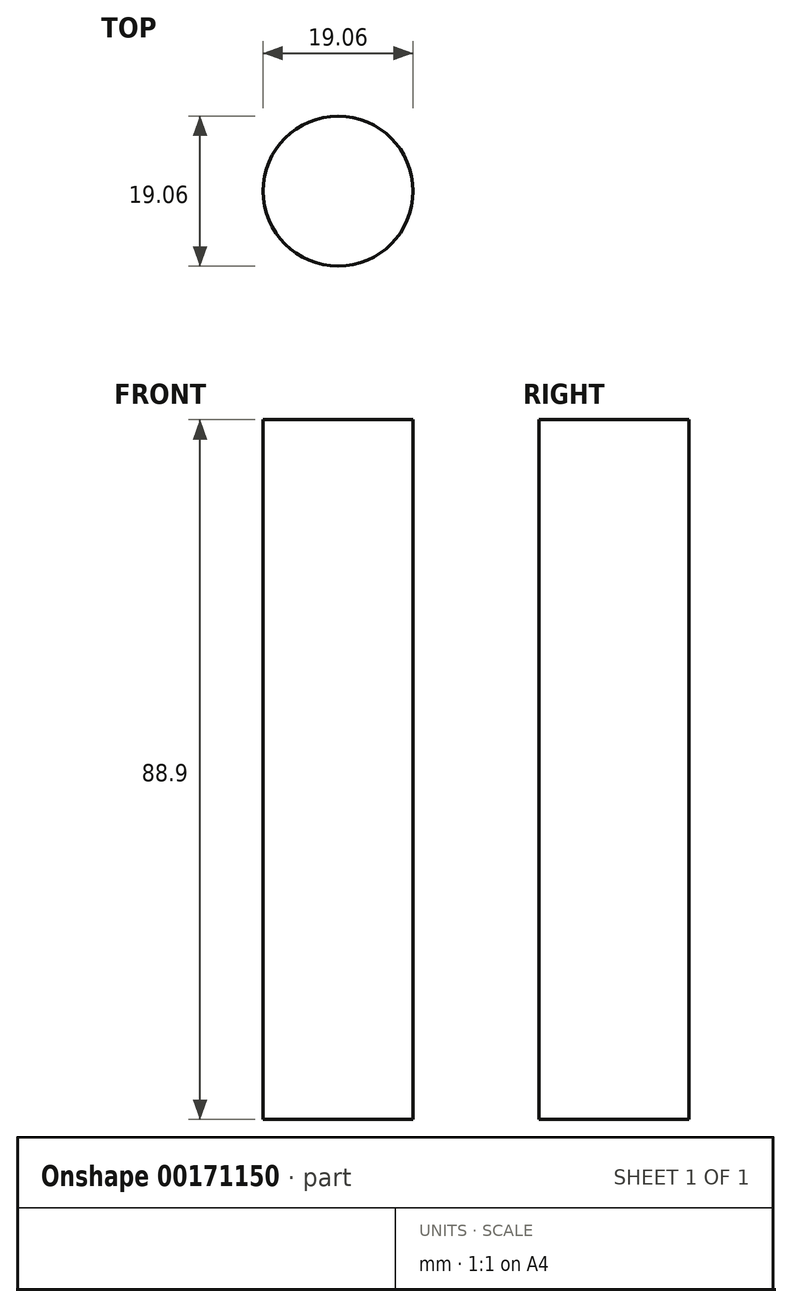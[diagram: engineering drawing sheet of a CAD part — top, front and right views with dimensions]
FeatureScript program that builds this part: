
annotation { "Feature Type Name" : "Feature", "Feature Type Description" : "" }
export const myFeature = defineFeature(function(context is Context, id is Id, definition is map)
    precondition{}
    {
        {
            var Q0;
            Q0=qCreatedBy(makeId("Top.planeOp"),FACE);
            var sketch = newSketch(context, id + "F0", { "sketchPlane" : qUnion([Q0])});
            skCircle(sketch, "E0", {"center": v(0, 0) * mm, "radius": 9.53 * mm});
            skSolve(sketch);
        }
        {
            var Q0;
            Q0=makeQuery(id+"F0.imprint","IMPRINT",FACE,{"disambiguationData":[TD([[makeQuery(id+"F0.imprint","IMPRINT",EDGE,{"derivedFrom":sQuery(id+"F0.wireOp",EDGE,"E0")}),1.0]])]});
            extrude(context, id + "F1", {"entities" : qUnion([Q0]), "oppositeDirection" : true, "depth" : 88.9 * mm});
        }
    });
